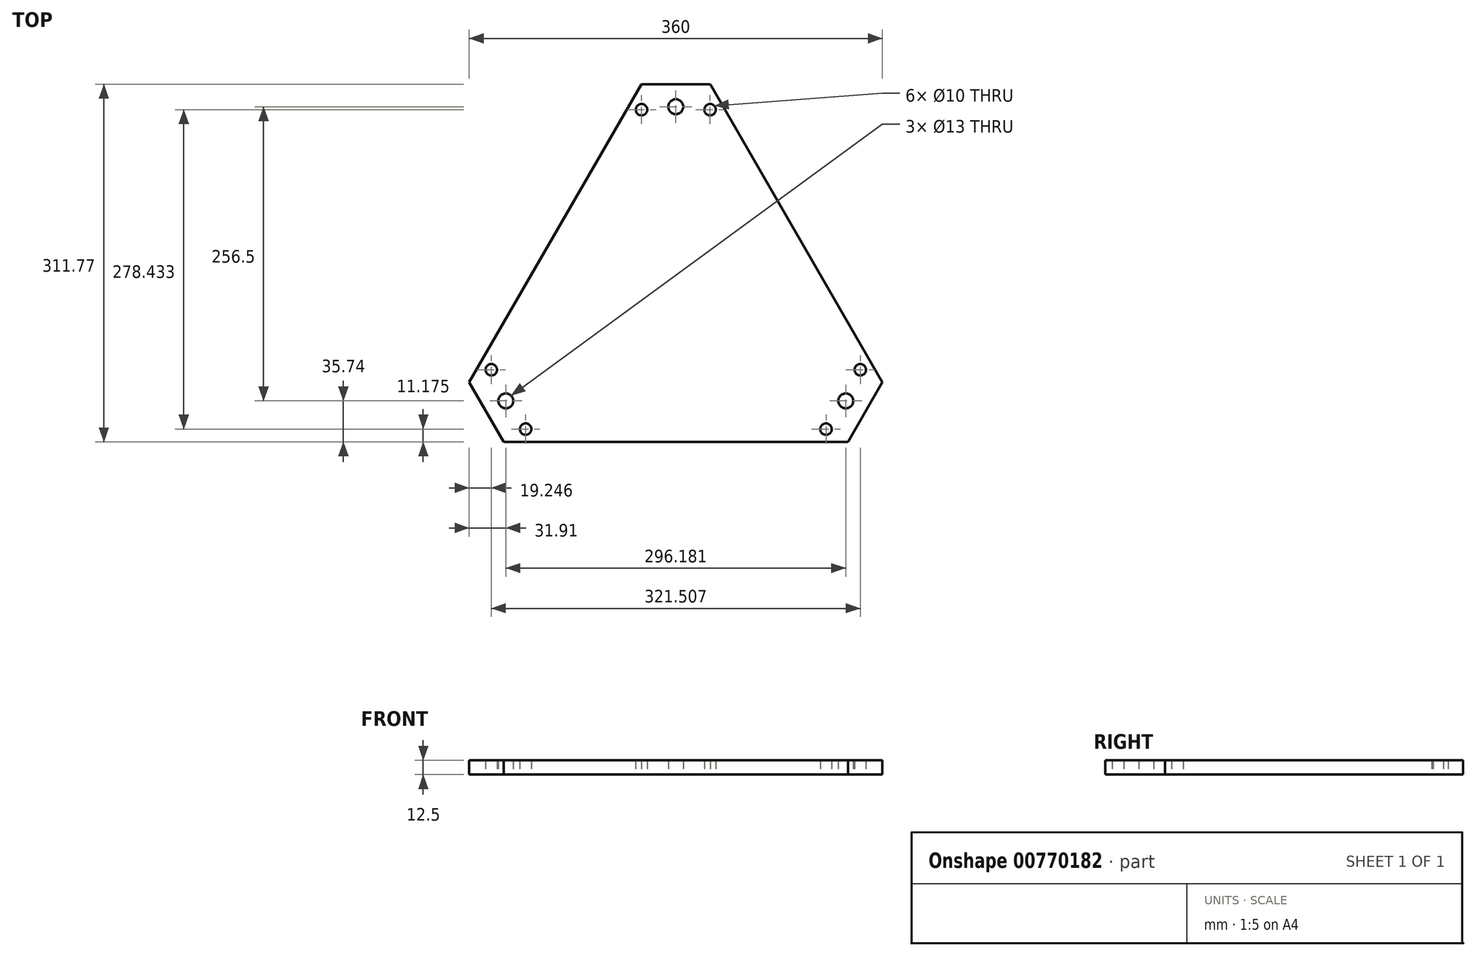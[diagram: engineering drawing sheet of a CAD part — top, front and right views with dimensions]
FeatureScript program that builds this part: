
annotation { "Feature Type Name" : "Feature", "Feature Type Description" : "" }
export const myFeature = defineFeature(function(context is Context, id is Id, definition is map)
    precondition{}
    {
        {
            var Q0;
            Q0=qCreatedBy(makeId("Top.planeOp"),FACE);
            var sketch = newSketch(context, id + "F0", { "sketchPlane" : qUnion([Q0])});
            skPoint(sketch, "E0", {"position": v(0, 0) * mm});
            skCircle(sketch, "E1", {"center": v(0, 0) * mm, "radius": 171 * mm, "construction": true});
            skLineSegment(sketch, "E2", {"start": v(0, 0) * mm, "end": v(0, 171) * mm, "construction": true});
            skLineSegment(sketch, "E3", {"start": v(0, 0) * mm, "end": v(148.1, -85.5) * mm, "construction": true});
            skLineSegment(sketch, "E4", {"start": v(0, 0) * mm, "end": v(-148.1, -85.5) * mm, "construction": true});
            skCircle(sketch, "E5", {"center": v(-148.1, -85.5) * mm, "radius": 6.5 * mm});
            skCircle(sketch, "E6", {"center": v(-160.75, -58.3) * mm, "radius": 5 * mm});
            skCircle(sketch, "E7", {"center": v(-130.87, -110.06) * mm, "radius": 5 * mm});
            skLineSegment(sketch, "E8", {"start": v(0, 0) * mm, "end": v(-160.75, -58.3) * mm, "construction": true});
            skLineSegment(sketch, "E9", {"start": v(0, 0) * mm, "end": v(-130.87, -110.06) * mm, "construction": true});
            skCircle(sketch, "E10.1.0", {"center": v(130.87, -110.06) * mm, "radius": 5 * mm});
            skCircle(sketch, "E10.1.1", {"center": v(148.1, -85.5) * mm, "radius": 6.5 * mm});
            skCircle(sketch, "E10.1.2", {"center": v(160.75, -58.3) * mm, "radius": 5 * mm});
            skLineSegment(sketch, "E10.1.3", {"start": v(0, 0) * mm, "end": v(160.75, -58.3) * mm, "construction": true});
            skLineSegment(sketch, "E10.1.5", {"start": v(0, 0) * mm, "end": v(130.87, -110.06) * mm, "construction": true});
            skCircle(sketch, "E10.2.0", {"center": v(29.88, 168.37) * mm, "radius": 5 * mm});
            skCircle(sketch, "E10.2.1", {"center": v(0, 171) * mm, "radius": 6.5 * mm});
            skCircle(sketch, "E10.2.2", {"center": v(-29.88, 168.37) * mm, "radius": 5 * mm});
            skLineSegment(sketch, "E10.2.3", {"start": v(0, 0) * mm, "end": v(-29.88, 168.37) * mm, "construction": true});
            skLineSegment(sketch, "E10.2.5", {"start": v(0, 0) * mm, "end": v(29.88, 168.37) * mm, "construction": true});
            skLineSegment(sketch, "E11", {"start": v(-180, -69.28) * mm, "end": v(-150, -121.24) * mm});
            skLineSegment(sketch, "E12", {"start": v(-150, -121.24) * mm, "end": v(150, -121.24) * mm});
            skLineSegment(sketch, "E13", {"start": v(150, -121.24) * mm, "end": v(180, -69.28) * mm});
            skLineSegment(sketch, "E14", {"start": v(180, -69.28) * mm, "end": v(30, 190.53) * mm});
            skLineSegment(sketch, "E15", {"start": v(30, 190.53) * mm, "end": v(-30, 190.53) * mm});
            skLineSegment(sketch, "E16", {"start": v(-30, 190.53) * mm, "end": v(-180, -69.28) * mm});
            skLineSegment(sketch, "E17", {"start": v(165, -95.26) * mm, "end": v(-105, 60.62) * mm, "construction": true});
            skLineSegment(sketch, "E18", {"start": v(-165, -95.26) * mm, "end": v(105, 60.62) * mm, "construction": true});
            skLineSegment(sketch, "E19", {"start": v(0, 190.53) * mm, "end": v(0, -121.24) * mm, "construction": true});
            skCircle(sketch, "E20", {"center": v(-148.1, -85.5) * mm, "radius": 30 * mm, "construction": true});
            skSolve(sketch);
        }
        {
            var Q0;
            Q0=makeQuery(id+"F0.imprint","IMPRINT",FACE,{"disambiguationData":[TD([[makeQuery(id+"F0.imprint","IMPRINT",EDGE,{"derivedFrom":sQuery(id+"F0.wireOp",EDGE,"E5")}),-1.0]])]});
            extrude(context, id + "F1", {"entities" : qUnion([Q0]), "depth" : 12.5 * mm, "offsetDistance" : 25 * mm});
        }
    });
